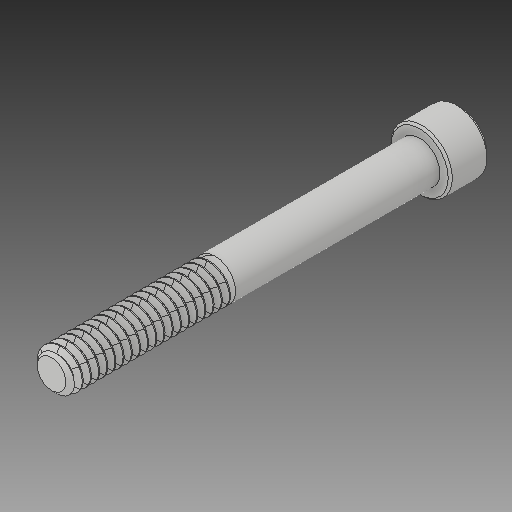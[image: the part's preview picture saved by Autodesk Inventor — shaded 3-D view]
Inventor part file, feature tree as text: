
AUTODESK INVENTOR PART (.ipt)
format: ipt  version: 2017 SP1 (Build 210196100, 196)  size: 613,888 bytes
history: native  units: in
note: dims shown in document units (in); Inventor stores cm internally (conversion verified against a paired STEP export)
features: chamfer x1
ambient origin geometry x8: Origin, YZ Plane, XZ Plane, XY Plane, X Axis, Y Axis, Z Axis, Center Point
bodies: Solid1 (feature_tree)
feature tree (1):
  chamfer  "Chamfer2"  [1 undecoded]
note: 1 required parameter value undecoded (feature->parameter linkage not recoverable at this tier; creation-order binding heuristic only, values carry confidence <= 0.55)
